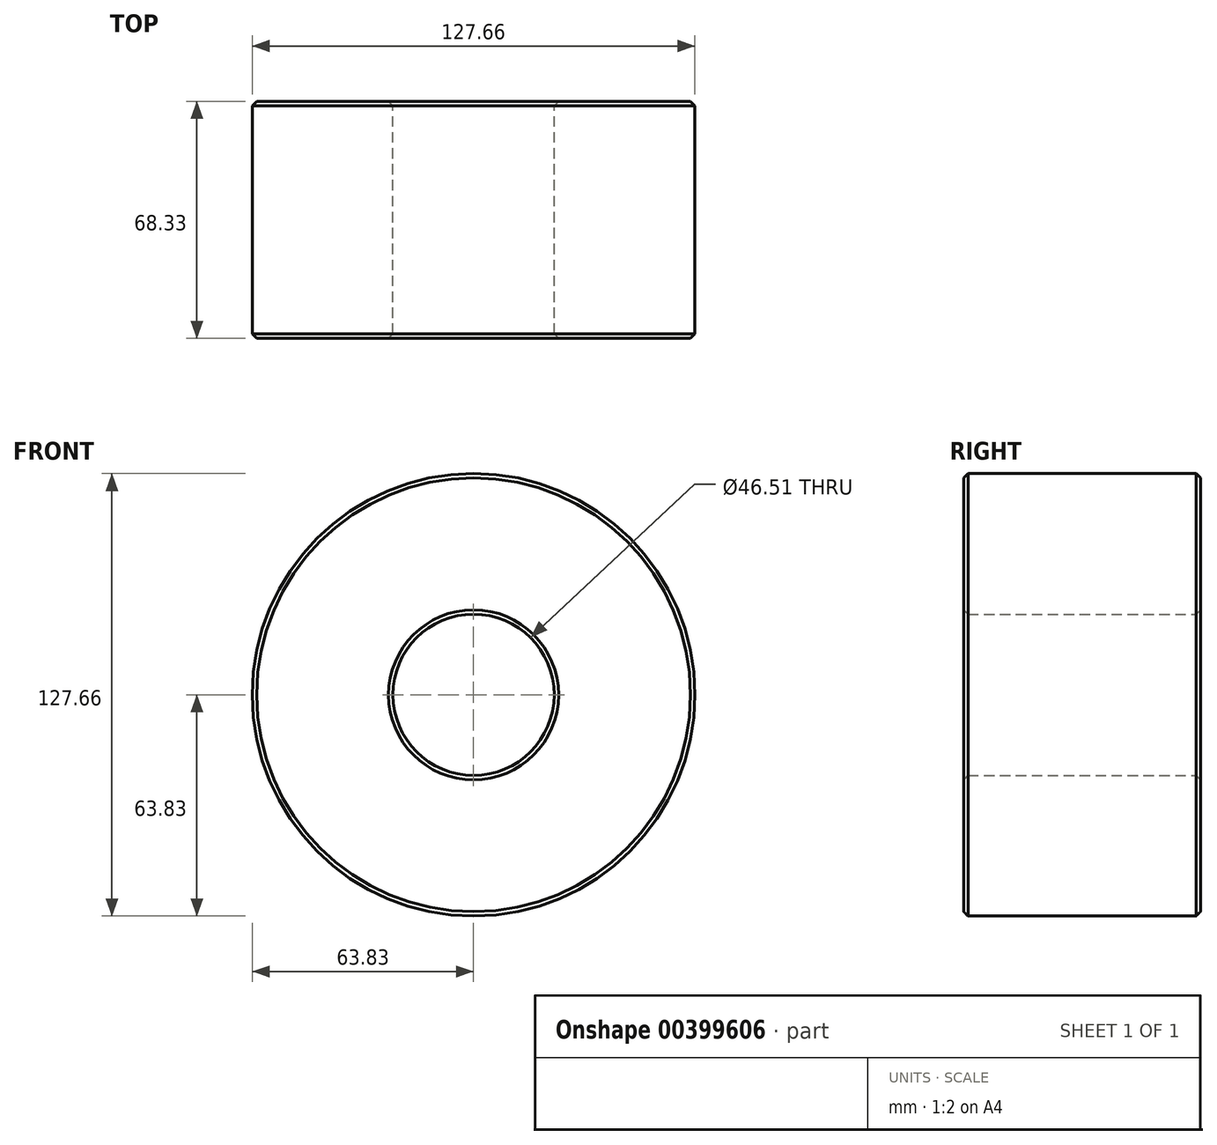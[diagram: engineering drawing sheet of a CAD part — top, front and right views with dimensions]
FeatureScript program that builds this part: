
annotation { "Feature Type Name" : "Feature", "Feature Type Description" : "" }
export const myFeature = defineFeature(function(context is Context, id is Id, definition is map)
    precondition{}
    {
        {
            var Q0;
            Q0=qCreatedBy(makeId("Front.planeOp"),FACE);
            var sketch = newSketch(context, id + "F0", { "sketchPlane" : qUnion([Q0])});
            skCircle(sketch, "E0", {"center": v(0, 0) * mm, "radius": 63.83 * mm});
            skCircle(sketch, "E1", {"center": v(0, 0) * mm, "radius": 23.25 * mm});
            skSolve(sketch);
        }
        {
            var Q0;
            Q0 = qSketchRegion(id + "F0", true);
            extrude(context, id + "F1", {"entities" : qUnion([Q0]), "depth" : 68.33 * mm});
        }
        {
            var Q0;
            Q0=makeQuery(id+"F1.opExtrude","SWEPT_FACE",FACE,{"disambiguationData":[OSD([sQuery(id+"F0.wireOp",EDGE,"E1")])]});
            var Q1;
            Q1=makeQuery(id+"F1.opExtrude","CAP_FACE",FACE,{"disambiguationData":[OSD([sQuery(id+"F0.wireOp",EDGE,"E0"),sQuery(id+"F0.wireOp",EDGE,"E1")])],"isStart":false});
            var Q2;
            Q2=makeQuery(id+"F1.opExtrude","CAP_EDGE",EDGE,{"disambiguationData":[OSD([sQuery(id+"F0.wireOp",EDGE,"E0")])],"isStart":true});
            chamfer(context, id + "F2", {"entities" : qUnion([Q0, Q1, Q2]), "width" : 1.27 * mm, "tangentPropagation" : true});
        }
    });
